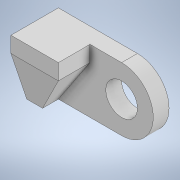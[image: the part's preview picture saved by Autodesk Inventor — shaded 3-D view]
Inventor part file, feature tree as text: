
AUTODESK INVENTOR PART (.ipt)
format: ipt  version: 2020 (Build 240168000, 168)  size: 133,120 bytes
history: native  units: mm
features: sketch x3, extrude x2, other x1, loft x1
ambient origin geometry x8: Origin, YZ Plane, XZ Plane, XY Plane, X Axis, Y Axis, Z Axis, Center Point
bodies: Body1 (feature_tree)
feature tree (7):
  other  "實體1"
  extrude  "擠出1"  Depth=70.0mm
  extrude  "擠出2"  Depth=40.0mm
  loft  "斷面混成1"
  sketch  "草圖1"
  sketch  "草圖2"
  sketch  "草圖4"
